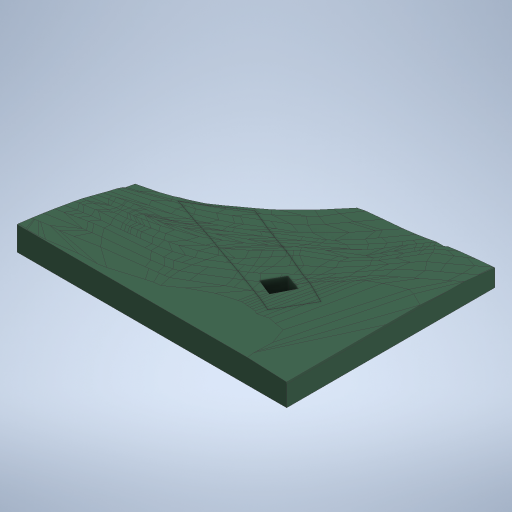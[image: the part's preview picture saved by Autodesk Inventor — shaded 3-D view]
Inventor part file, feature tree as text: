
AUTODESK INVENTOR PART (.ipt)
format: ipt  version: 2024 (Build 280153020, 153B)  size: 2,477,056 bytes
history: native  units: in
note: dims shown in document units (in); Inventor stores cm internally (conversion verified against a paired STEP export)
features: sketch x16, loft x14, extrude x2, other x1
ambient origin geometry x8: Origin, YZ Plane, XZ Plane, XY Plane, X Axis, Y Axis, Z Axis, Center Point
bodies: Solid1 (feature_tree)
feature tree (33):
  sketch  "Sketch1"  dims[d18=1207.1141in d21=1046.865in]
  sketch  "Sketch2"  dims[d23=301.0in d24=0.4423in]
  sketch  "Sketch3"  dims[d30=4896.0in d33=4920.0in d34=4944.0in d35=4968.0in d36=4992.0in d37=5016.0in]
  sketch  "Sketch4"  dims[d38=5040.0in d39=5064.0in]
  sketch  "Sketch5"  dims[d40=5088.0in d41=5112.0in]
  sketch  "Sketch6"  dims[d42=5136.0in d43=5160.0in]
  sketch  "Sketch7"  dims[d44=5184.0in d45=5208.0in]
  sketch  "Sketch8"  dims[d46=5232.0in d47=0.0in d48=90.0deg]
  sketch  "Sketch9"  dims[d49=0.0in d50=90.0deg d52=0.0in d53=90.0deg]
  sketch  "Sketch10"  dims[d54=0.0in d55=90.0deg d56=0.0in d57=90.0deg]
  sketch  "Sketch11"  dims[d58=0.0in d59=90.0deg d60=0.0in d61=90.0deg]
  sketch  "Sketch12"  dims[d62=0.0in d63=90.0deg d64=0.0in d65=90.0deg]
  sketch  "Sketch13"  dims[d66=0.0in d67=90.0deg d68=0.0in d69=90.0deg]
  sketch  "Sketch14"  dims[d70=0.0in d71=90.0deg d72=0.0in d73=90.0deg]
  sketch  "Sketch15"  dims[d74=0.0in d75=90.0deg d93=0.0in d94=90.0deg]
  loft  "408_To_410"
  loft  "410_To_412"
  loft  "412_To_414"
  loft  "414_To_416"
  loft  "416_To_418"
  loft  "418_To_420"
  loft  "420_To_422"
  loft  "422_To_424"
  loft  "424_To_426"
  loft  "426_To_428"
  loft  "428_To_430"
  loft  "430_To_432"
  loft  "432_To_434"
  loft  "434_To_436"
  extrude  "Extrusion2"  TaperAngle=0.0deg  [1 undecoded]
  extrude  "Extrusion3"  TaperAngle=0.0deg  [1 undecoded]
  other  "Image1"
  sketch  "Sketch17"  dims[d95=0.0in d96=90.0deg d97=0.0in d98=90.0deg d99=0.0in d100=90.0deg d106=0.0in d107=90.0deg d108=0.0in d109=90.0deg d110=0.0in d111=90.0deg d112=0.0in d113=90.0deg d114=0.0in d115=90.0deg d116=0.0in d117=90.0deg d122=4.5in d123=0.0in d124=0.0in d125=0.0in d126=90.0deg d127=0.0in d128=90.0deg d135=0.0in d136=90.0deg d137=0.0in d138=90.0deg d142=1.0in d143=0.0in d26=0.5in d27=0.0344in d28=0.5in d29=0.0344in]
note: 2 required parameter values undecoded (feature->parameter linkage not recoverable at this tier; creation-order binding heuristic only, values carry confidence <= 0.55)
